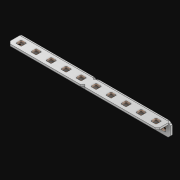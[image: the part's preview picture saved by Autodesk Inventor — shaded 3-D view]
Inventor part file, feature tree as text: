
AUTODESK INVENTOR PART (.ipt)
format: ipt  version: 2021 (Build 250183000, 183)  size: 615,424 bytes
history: native  units: in
note: dims shown in document units (in); Inventor stores cm internally (conversion verified against a paired STEP export)
features: extrude x21, other x20, sketch x3, pattern_linear x1, sheet_metal_op x1
ambient origin geometry x8: Origin, YZ Plane, XZ Plane, XY Plane, X Axis, Y Axis, Z Axis, Center Point
bodies: Solid1 (feature_tree)
feature tree (46):
  pattern_linear  "Rectangular Pattern1"  Spacing1=0.063in  [1 undecoded]
  extrude  "Extrusion1"  Depth=0.5in
  sketch  "Sketch1"  dims[d0=0.182in]
  other  "Srf1"
  sketch  "Sketch2"  dims[d1=0.063in d2=0.0in]
  other  "Srf2"
  other  "Srf3"
  other  "Srf5"
  other  "Srf7"
  other  "Srf9"
  other  "Srf11"
  other  "Srf13"
  other  "Srf15"
  other  "Srf17"
  other  "Srf19"
  other  "Srf4"
  other  "Srf6"
  other  "Srf8"
  other  "Srf10"
  other  "Srf12"
  other  "Srf14"
  other  "Srf16"
  other  "Srf18"
  other  "Srf20"
  sketch  "Sketch3"  dims[d3=0.182in d4=0.063in d5=0.0in d8=0.5in d9=12.5in d10=0.0in]
  sheet_metal_op  "Fold1"
  extrude  "ExtrusionSrf1"  Depth=0.5in TaperAngle=0.0deg
  extrude  "ExtrusionSrf2"  [1 undecoded]
  extrude  "ExtrusionSrf3"  [1 undecoded]
  extrude  "ExtrusionSrf4"  [1 undecoded]
  extrude  "ExtrusionSrf5"  [1 undecoded]
  extrude  "ExtrusionSrf6"  [1 undecoded]
  extrude  "ExtrusionSrf7"  [1 undecoded]
  extrude  "ExtrusionSrf8"  [1 undecoded]
  extrude  "ExtrusionSrf9"  [1 undecoded]
  extrude  "ExtrusionSrf10"  [1 undecoded]
  extrude  "ExtrusionSrf11"  [1 undecoded]
  extrude  "ExtrusionSrf37"  [1 undecoded]
  extrude  "ExtrusionSrf38"  [1 undecoded]
  extrude  "ExtrusionSrf39"  [1 undecoded]
  extrude  "ExtrusionSrf40"  [1 undecoded]
  extrude  "ExtrusionSrf41"  [1 undecoded]
  extrude  "ExtrusionSrf42"  [1 undecoded]
  extrude  "ExtrusionSrf43"  [1 undecoded]
  extrude  "ExtrusionSrf44"  [1 undecoded]
  extrude  "ExtrusionSrf45"  [1 undecoded]
note: 20 required parameter values undecoded (feature->parameter linkage not recoverable at this tier; creation-order binding heuristic only, values carry confidence <= 0.55)
